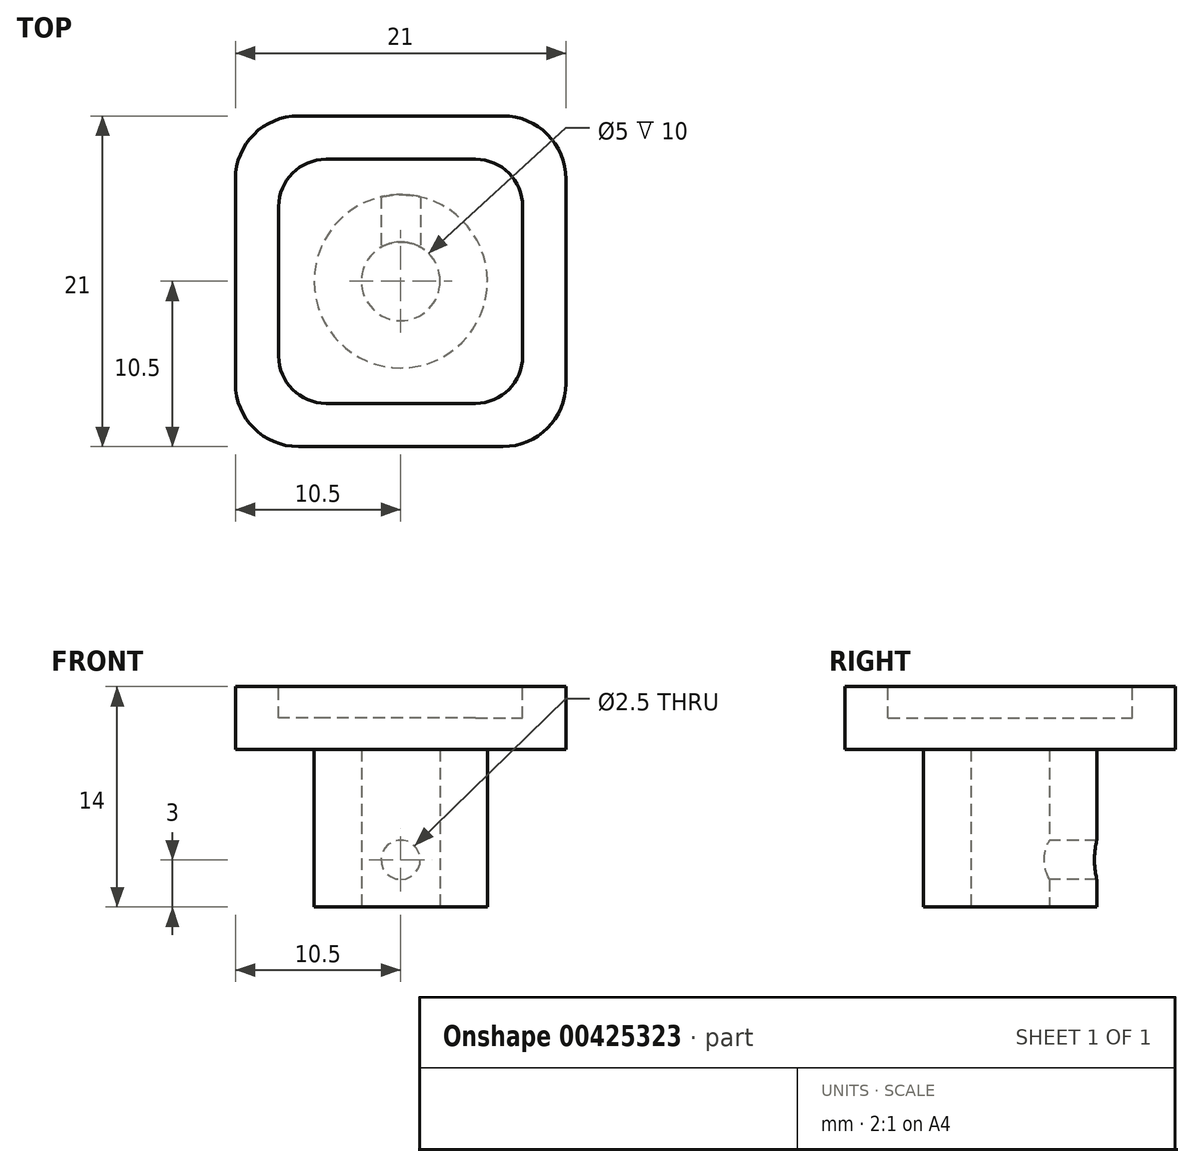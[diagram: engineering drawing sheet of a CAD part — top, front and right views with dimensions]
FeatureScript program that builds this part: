
annotation { "Feature Type Name" : "Feature", "Feature Type Description" : "" }
export const myFeature = defineFeature(function(context is Context, id is Id, definition is map)
    precondition{}
    {
        {
            var Q0;
            Q0=qCreatedBy(makeId("Top.planeOp"),FACE);
            var sketch = newSketch(context, id + "F0", { "sketchPlane" : qUnion([Q0])});
            skCircle(sketch, "E0", {"center": v(0, 0) * mm, "radius": 2.5 * mm});
            skCircle(sketch, "E1", {"center": v(0, 0) * mm, "radius": 5.5 * mm});
            skSolve(sketch);
        }
        {
            var Q0;
            Q0=qSketchRegion(id+"F0",true);
            extrude(context, id + "F1", {"entities" : qUnion([Q0]), "depth" : 10 * mm});
        }
        {
            var Q0;
            Q0=makeQuery(id+"F1.opExtrude","CAP_FACE",FACE,{"disambiguationData":[OSD([sQuery(id+"F0.wireOp",EDGE,"E0"),sQuery(id+"F0.wireOp",EDGE,"E1")])],"isStart":false});
            var sketch = newSketch(context, id + "F2", { "sketchPlane" : qUnion([Q0])});
            skLineSegment(sketch, "E2.bottom", {"start": v(10.5, -10.5) * mm, "end": v(-10.5, -10.5) * mm});
            skLineSegment(sketch, "E2.top", {"start": v(10.5, 10.5) * mm, "end": v(-10.5, 10.5) * mm});
            skLineSegment(sketch, "E2.left", {"start": v(10.5, -10.5) * mm, "end": v(10.5, 10.5) * mm});
            skLineSegment(sketch, "E2.right", {"start": v(-10.5, -10.5) * mm, "end": v(-10.5, 10.5) * mm});
            skPoint(sketch, "E2.middle", {"position": v(0, 0) * mm});
            skSolve(sketch);
        }
        {
            var Q0;
            Q0=qSketchRegion(id+"F2",true);
            extrude(context, id + "F3", {"entities" : qUnion([Q0]), "operationType" : NewBodyOperationType.ADD, "depth" : 4 * mm});
        }
        {
            var Q0;
            Q0=makeQuery(id+"F3.opExtrude","CAP_FACE",FACE,{"disambiguationData":[OSD([sQuery(id+"F2.wireOp",EDGE,"E2.bottom"),sQuery(id+"F2.wireOp",EDGE,"E2.top"),sQuery(id+"F2.wireOp",EDGE,"E2.left"),sQuery(id+"F2.wireOp",EDGE,"E2.right")])],"isStart":false});
            var sketch = newSketch(context, id + "F4", { "sketchPlane" : qUnion([Q0])});
            skLineSegment(sketch, "E3.bottom", {"start": v(7.75, -7.75) * mm, "end": v(-7.75, -7.75) * mm});
            skLineSegment(sketch, "E3.top", {"start": v(7.75, 7.75) * mm, "end": v(-7.75, 7.75) * mm});
            skLineSegment(sketch, "E3.left", {"start": v(7.75, -7.75) * mm, "end": v(7.75, 7.75) * mm});
            skLineSegment(sketch, "E3.right", {"start": v(-7.75, -7.75) * mm, "end": v(-7.75, 7.75) * mm});
            skPoint(sketch, "E3.middle", {"position": v(0, 0) * mm});
            skSolve(sketch);
        }
        {
            var Q0;
            Q0=qSketchRegion(id+"F4",true);
            extrude(context, id + "F5", {"entities" : qUnion([Q0]), "operationType" : NewBodyOperationType.REMOVE, "oppositeDirection" : true, "depth" : 2 * mm});
        }
        {
            var Q0;
            Q0=makeQuery(id+"F3.opExtrude","SWEPT_EDGE",EDGE,{"disambiguationData":[OSD([sQuery(id+"F2.wireOp",EDGE,"E2.top"),sQuery(id+"F2.wireOp",EDGE,"E2.left")])]});
            var Q1;
            Q1=makeQuery(id+"F3.opExtrude","SWEPT_EDGE",EDGE,{"disambiguationData":[OSD([sQuery(id+"F2.wireOp",EDGE,"E2.bottom"),sQuery(id+"F2.wireOp",EDGE,"E2.left")])]});
            var Q2;
            Q2=makeQuery(id+"F3.opExtrude","SWEPT_EDGE",EDGE,{"disambiguationData":[OSD([sQuery(id+"F2.wireOp",EDGE,"E2.bottom"),sQuery(id+"F2.wireOp",EDGE,"E2.right")])]});
            var Q3;
            Q3=makeQuery(id+"F3.opExtrude","SWEPT_EDGE",EDGE,{"disambiguationData":[OSD([sQuery(id+"F2.wireOp",EDGE,"E2.top"),sQuery(id+"F2.wireOp",EDGE,"E2.right")])]});
            fillet(context, id + "F6", {"entities" : qUnion([Q0, Q1, Q2, Q3]), "radius" : 4 * mm, "tangentPropagation" : true, "allowEdgeOverflow" : false});
        }
        {
            var Q0;
            Q0=qCreatedBy(makeId("Front.planeOp"),FACE);
            var sketch = newSketch(context, id + "F7", { "sketchPlane" : qUnion([Q0])});
            skCircle(sketch, "E4", {"center": v(0, 3) * mm, "radius": 1.25 * mm});
            skSolve(sketch);
        }
        {
            var Q0;
            Q0=qSketchRegion(id+"F7",true);
            extrude(context, id + "F8", {"entities" : qUnion([Q0]), "operationType" : NewBodyOperationType.REMOVE, "oppositeDirection" : true, "depth" : 10 * mm});
        }
        {
            var Q0;
            Q0=makeQuery(id+"F5.boolean.opBoolean","COPY",EDGE,{"derivedFrom":makeQuery(id+"F5.opExtrude","SWEPT_EDGE",EDGE,{"disambiguationData":[OSD([sQuery(id+"F4.wireOp",EDGE,"E3.top"),sQuery(id+"F4.wireOp",EDGE,"E3.right")])]})});
            var Q1;
            Q1=makeQuery(id+"F5.boolean.opBoolean","COPY",EDGE,{"derivedFrom":makeQuery(id+"F5.opExtrude","SWEPT_EDGE",EDGE,{"disambiguationData":[OSD([sQuery(id+"F4.wireOp",EDGE,"E3.top"),sQuery(id+"F4.wireOp",EDGE,"E3.left")])]})});
            var Q2;
            Q2=makeQuery(id+"F5.boolean.opBoolean","COPY",EDGE,{"derivedFrom":makeQuery(id+"F5.opExtrude","SWEPT_EDGE",EDGE,{"disambiguationData":[OSD([sQuery(id+"F4.wireOp",EDGE,"E3.bottom"),sQuery(id+"F4.wireOp",EDGE,"E3.right")])]})});
            var Q3;
            Q3=makeQuery(id+"F5.boolean.opBoolean","COPY",EDGE,{"derivedFrom":makeQuery(id+"F5.opExtrude","SWEPT_EDGE",EDGE,{"disambiguationData":[OSD([sQuery(id+"F4.wireOp",EDGE,"E3.bottom"),sQuery(id+"F4.wireOp",EDGE,"E3.left")])]})});
            var Q4;
            Q4=makeQuery(id+"F1.opExtrude","CAP_EDGE",EDGE,{"disambiguationData":[OSD([sQuery(id+"F0.wireOp",EDGE,"E1")])],"isStart":false});
            fillet(context, id + "F9", {"entities" : qUnion([Q0, Q1, Q2, Q3, Q4]), "radius" : 3 * mm, "tangentPropagation" : true, "allowEdgeOverflow" : false});
        }
    });
